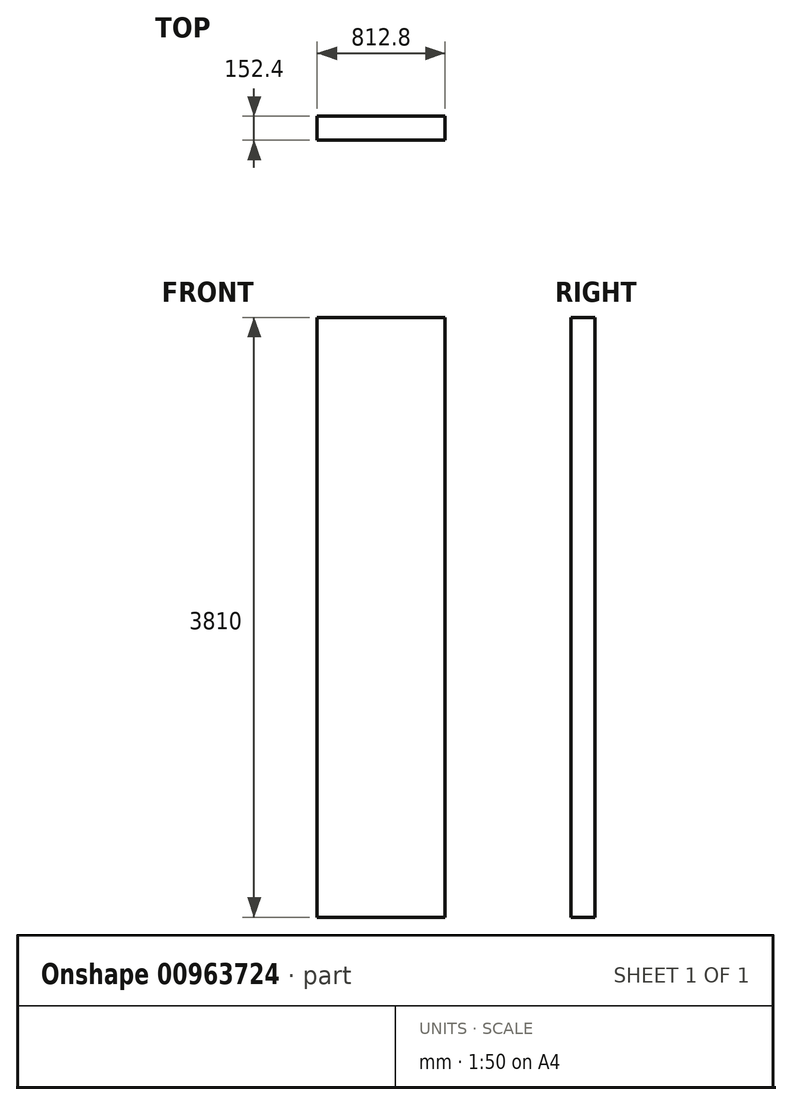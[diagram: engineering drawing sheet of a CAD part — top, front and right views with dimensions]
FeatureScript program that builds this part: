
annotation { "Feature Type Name" : "Feature", "Feature Type Description" : "" }
export const myFeature = defineFeature(function(context is Context, id is Id, definition is map)
    precondition{}
    {
        {
            var Q0;
            Q0=qCreatedBy(makeId("Front.planeOp"),FACE);
            var sketch = newSketch(context, id + "F0", { "sketchPlane" : qUnion([Q0])});
            skLineSegment(sketch, "E0.bottom", {"start": v(-363.95, 3333.32) * mm, "end": v(448.85, 3333.32) * mm});
            skLineSegment(sketch, "E0.top", {"start": v(-363.95, -476.68) * mm, "end": v(448.85, -476.68) * mm});
            skLineSegment(sketch, "E0.left", {"start": v(-363.95, 3333.32) * mm, "end": v(-363.95, -476.68) * mm});
            skLineSegment(sketch, "E0.right", {"start": v(448.85, 3333.32) * mm, "end": v(448.85, -476.68) * mm});
            skSolve(sketch);
        }
        {
            var Q0;
            Q0=makeQuery(id+"F0.imprint","IMPRINT",FACE,{"disambiguationData":[TD([[makeQuery(id+"F0.imprint","IMPRINT",EDGE,{"derivedFrom":sQuery(id+"F0.wireOp",EDGE,"E0.bottom")}),-1.0]])]});
            extrude(context, id + "F1", {"entities" : qUnion([Q0]), "depth" : 152.4 * mm, "offsetDistance" : 25.4 * mm});
        }
    });
